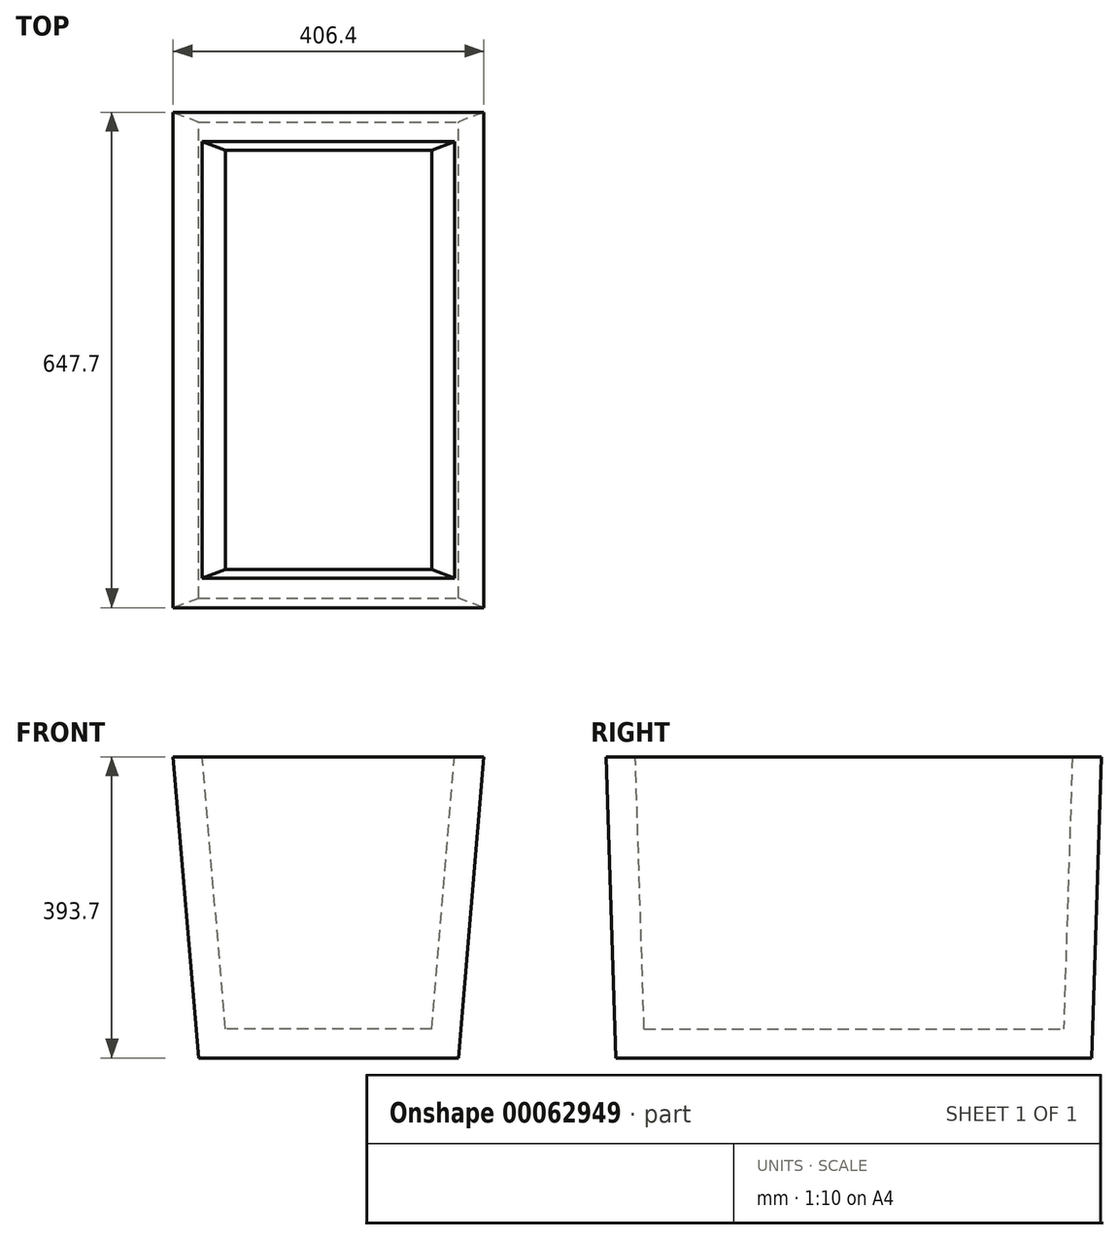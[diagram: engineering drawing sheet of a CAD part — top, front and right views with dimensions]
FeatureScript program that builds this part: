
annotation { "Feature Type Name" : "Feature", "Feature Type Description" : "" }
export const myFeature = defineFeature(function(context is Context, id is Id, definition is map)
    precondition{}
    {
        {
            var Q0;
            Q0=qCreatedBy(makeId("Top.planeOp"),FACE);
            cPlane(context, id + "F0", {"entities" : qUnion([Q0]), "cplaneType" : CPlaneType.OFFSET, "offset" : 393.7 * mm, "width" : 152.4 * mm, "height" : 152.4 * mm});
        }
        {
            var Q0;
            Q0=qCreatedBy(makeId("Top.planeOp"),FACE);
            var sketch = newSketch(context, id + "F1", { "sketchPlane" : qUnion([Q0])});
            skLineSegment(sketch, "E0.rect.bottom", {"start": v(-169.86, -311.15) * mm, "end": v(169.86, -311.15) * mm});
            skLineSegment(sketch, "E0.rect.top", {"start": v(-169.86, 311.15) * mm, "end": v(169.86, 311.15) * mm});
            skLineSegment(sketch, "E0.rect.left", {"start": v(-169.86, -311.15) * mm, "end": v(-169.86, 311.15) * mm});
            skLineSegment(sketch, "E0.rect.right", {"start": v(169.86, -311.15) * mm, "end": v(169.86, 311.15) * mm});
            skPoint(sketch, "E0.rect.middle", {"position": v(0, 0) * mm});
            skSolve(sketch);
        }
        {
            var Q0;
            Q0=qCreatedBy(id+"F0.planeOp",FACE);
            var sketch = newSketch(context, id + "F2", { "sketchPlane" : qUnion([Q0])});
            skLineSegment(sketch, "E1.rect.bottom", {"start": v(203.2, -323.85) * mm, "end": v(-203.2, -323.85) * mm});
            skLineSegment(sketch, "E1.rect.top", {"start": v(203.2, 323.85) * mm, "end": v(-203.2, 323.85) * mm});
            skLineSegment(sketch, "E1.rect.left", {"start": v(203.2, -323.85) * mm, "end": v(203.2, 323.85) * mm});
            skLineSegment(sketch, "E1.rect.right", {"start": v(-203.2, -323.85) * mm, "end": v(-203.2, 323.85) * mm});
            skPoint(sketch, "E1.rect.middle", {"position": v(0, 0) * mm});
            skSolve(sketch);
        }
        {
            var Q0;
            Q0=makeQuery(id+"F2.imprint","IMPRINT",FACE,{"disambiguationData":[TD([[makeQuery(id+"F2.imprint","IMPRINT",EDGE,{"derivedFrom":sQuery(id+"F2.wireOp",EDGE,"E1.rect.bottom")}),-1.0]])]});
            var Q1;
            Q1=makeQuery(id+"F1.imprint","IMPRINT",FACE,{"disambiguationData":[TD([[makeQuery(id+"F1.imprint","IMPRINT",EDGE,{"derivedFrom":sQuery(id+"F1.wireOp",EDGE,"E0.rect.bottom")}),1.0]])]});
            var Q2;
            Q2=sQuery(id+"F2.wireOp",VERTEX,"E1.rect.middle");
            var Q3;
            Q3=sQuery(id+"F1.wireOp",VERTEX,"E0.rect.middle");
            loft(context, id + "F3", {"sheetProfilesArray" : [{ "sheetProfileEntities" : qUnion([Q0]) }, { "sheetProfileEntities" : qUnion([Q1]) }], "connections" : [{ "connectionEntities" : qUnion([Q2, Q3]), "connectionEdgeQueries" : qUnion([]), "connectionEdgeParameters" : [] }]});
        }
        {
            var Q0;
            Q0=makeQuery(id+"F3.opLoft","CAP_FACE",FACE,{"disambiguationData":[OSD([makeQuery(id+"F2.imprint","IMPRINT",FACE,{"disambiguationData":[TD([[makeQuery(id+"F2.imprint","IMPRINT",EDGE,{"derivedFrom":sQuery(id+"F2.wireOp",EDGE,"E1.rect.bottom")}),-1.0]])]})])],"isStart":true});
            shell(context, id + "F4", {"entities" : qUnion([Q0]), "thickness" : 38.1 * mm});
        }
    });
